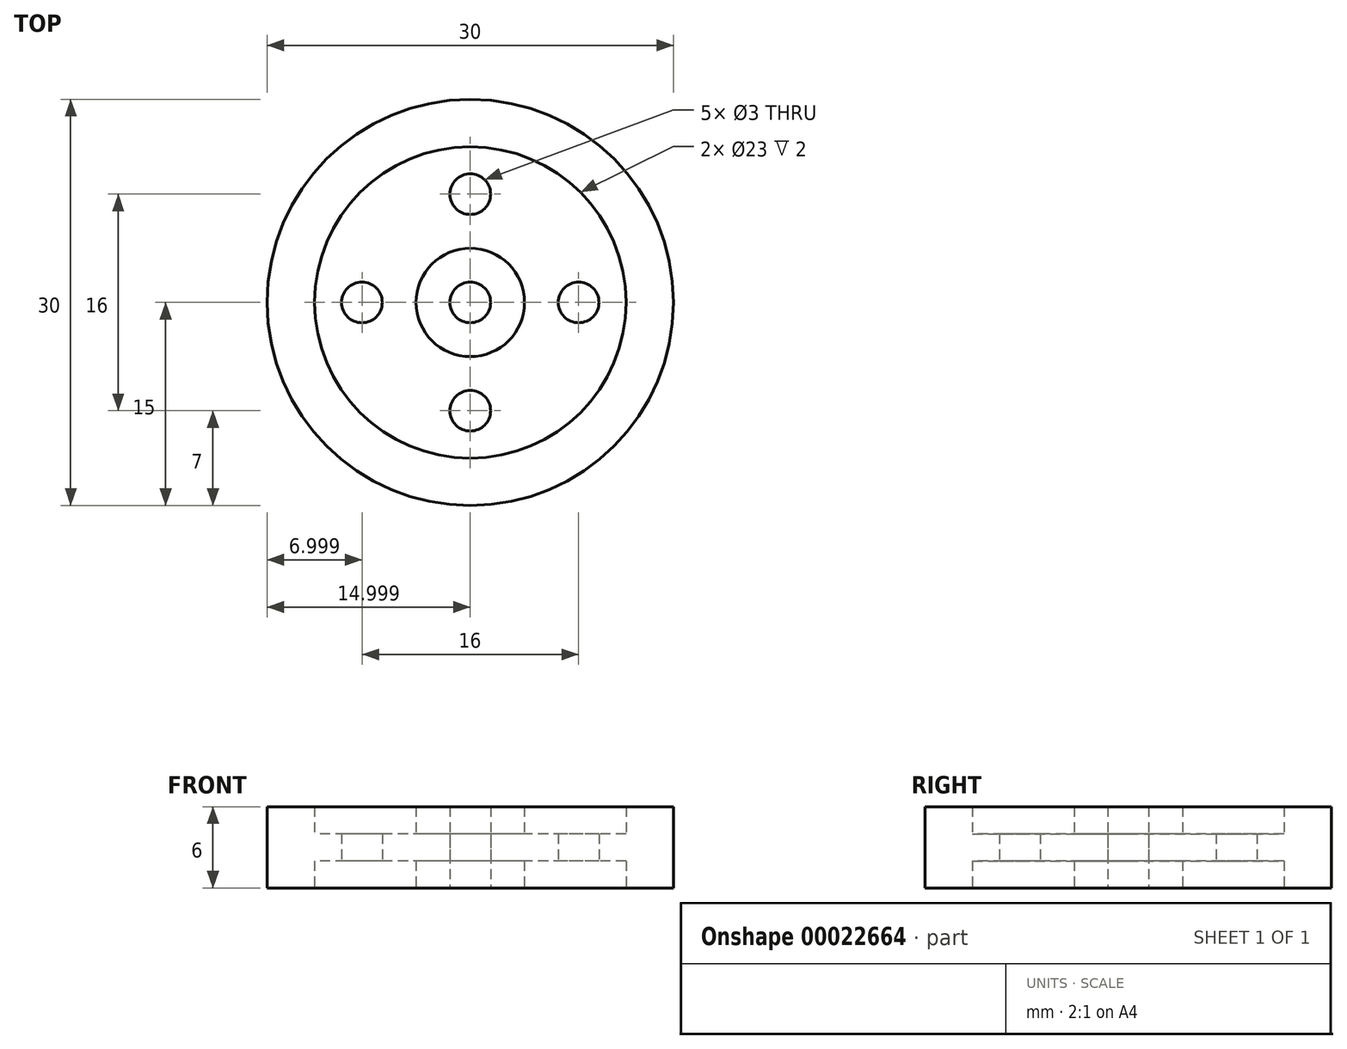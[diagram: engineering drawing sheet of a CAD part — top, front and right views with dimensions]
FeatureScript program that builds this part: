
annotation { "Feature Type Name" : "Feature", "Feature Type Description" : "" }
export const myFeature = defineFeature(function(context is Context, id is Id, definition is map)
    precondition{}
    {
        {
            var Q0;
            Q0=qCreatedBy(makeId("Top.planeOp"),FACE);
            var sketch = newSketch(context, id + "F0", { "sketchPlane" : qUnion([Q0])});
            skCircle(sketch, "E0", {"center": v(-37.6, 11.42) * mm, "radius": 15 * mm});
            skCircle(sketch, "E1", {"center": v(-37.6, 11.42) * mm, "radius": 11.5 * mm});
            skCircle(sketch, "E2", {"center": v(-37.6, 11.42) * mm, "radius": 4 * mm});
            skCircle(sketch, "E3", {"center": v(-37.6, 11.42) * mm, "radius": 1.5 * mm});
            skCircle(sketch, "E4", {"center": v(-37.6, 19.42) * mm, "radius": 1.5 * mm});
            skCircle(sketch, "E5.1.0", {"center": v(-45.6, 11.42) * mm, "radius": 1.5 * mm});
            skCircle(sketch, "E5.2.0", {"center": v(-37.6, 3.42) * mm, "radius": 1.5 * mm});
            skCircle(sketch, "E5.3.0", {"center": v(-29.6, 11.42) * mm, "radius": 1.5 * mm});
            skSolve(sketch);
        }
        {
            var Q0;
            Q0=makeQuery(id+"F0.imprint","IMPRINT",FACE,{"disambiguationData":[TD([[makeQuery(id+"F0.imprint","IMPRINT",EDGE,{"derivedFrom":sQuery(id+"F0.wireOp",EDGE,"E0")}),1.0]])]});
            var Q1;
            Q1=makeQuery(id+"F0.imprint","IMPRINT",FACE,{"disambiguationData":[TD([[makeQuery(id+"F0.imprint","IMPRINT",EDGE,{"derivedFrom":sQuery(id+"F0.wireOp",EDGE,"E2")}),1.0]])]});
            extrude(context, id + "F1", {"entities" : qUnion([Q0, Q1]), "depth" : 6 * mm});
        }
        {
            var Q0;
            Q0=makeQuery(id+"F0.imprint","IMPRINT",FACE,{"disambiguationData":[TD([[makeQuery(id+"F0.imprint","IMPRINT",EDGE,{"derivedFrom":sQuery(id+"F0.wireOp",EDGE,"E1")}),1.0]])]});
            extrude(context, id + "F2", {"entities" : qUnion([Q0]), "operationType" : NewBodyOperationType.ADD, "depth" : 4 * mm});
        }
        {
            var Q0;
            Q0=makeQuery(id+"F0.imprint","IMPRINT",FACE,{"disambiguationData":[TD([[makeQuery(id+"F0.imprint","IMPRINT",EDGE,{"derivedFrom":sQuery(id+"F0.wireOp",EDGE,"E1")}),1.0]])]});
            extrude(context, id + "F3", {"entities" : qUnion([Q0]), "operationType" : NewBodyOperationType.REMOVE, "depth" : 2 * mm});
        }
    });
